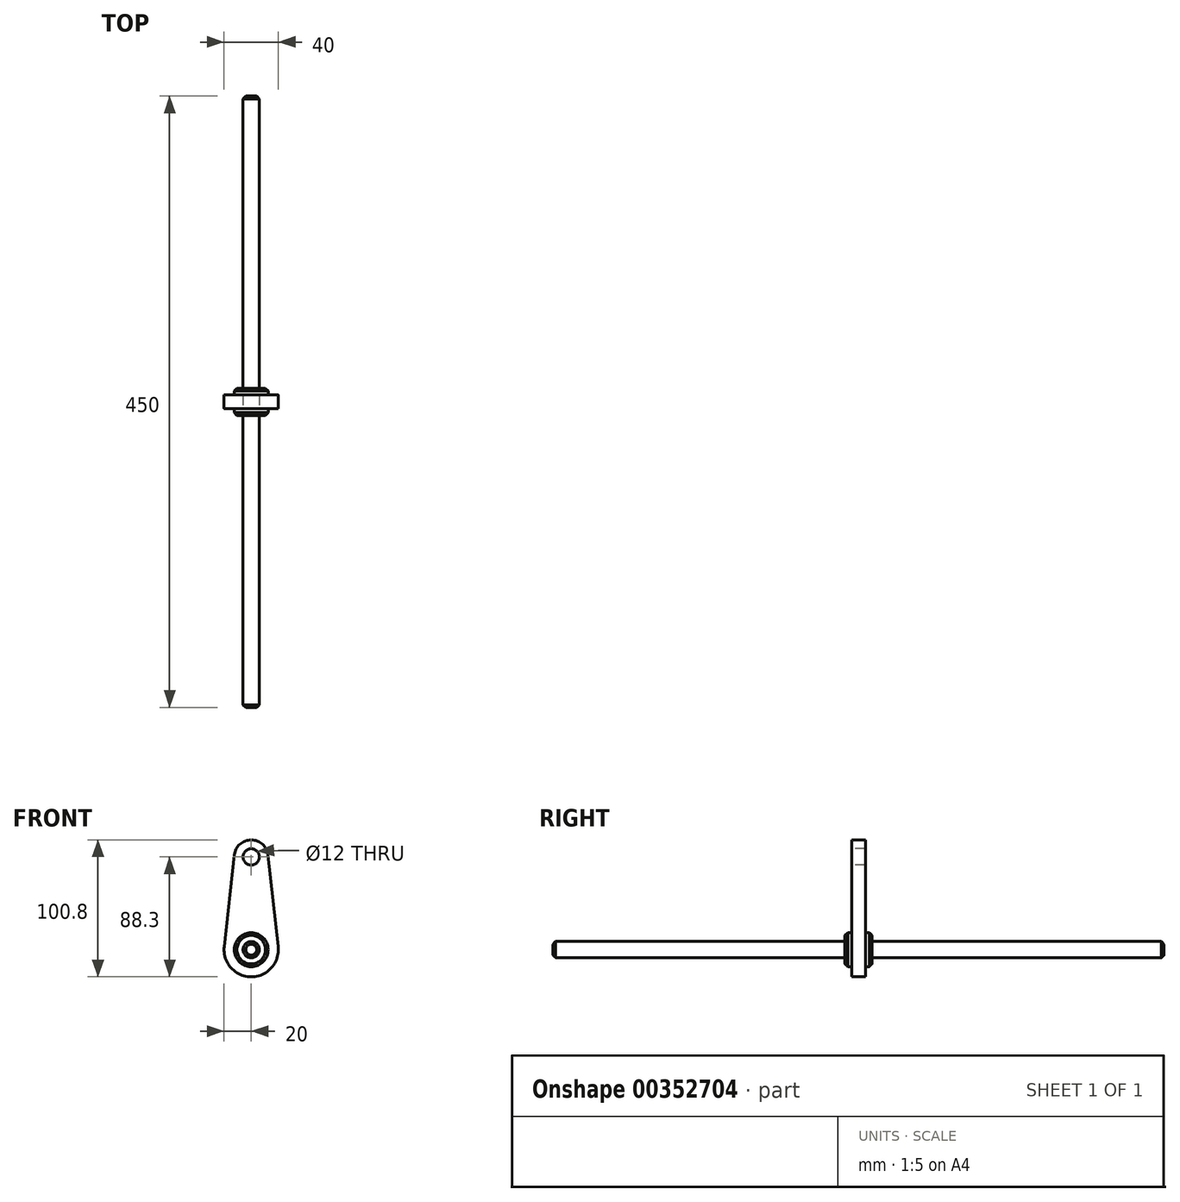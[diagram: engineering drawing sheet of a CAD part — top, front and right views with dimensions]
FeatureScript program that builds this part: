
annotation { "Feature Type Name" : "Feature", "Feature Type Description" : "" }
export const myFeature = defineFeature(function(context is Context, id is Id, definition is map)
    precondition{}
    {
        {
            var Q0;
            Q0=qCreatedBy(makeId("Front.planeOp"),FACE);
            var sketch = newSketch(context, id + "F0", { "sketchPlane" : qUnion([Q0])});
            skCircle(sketch, "E0", {"center": v(0, 0) * mm, "radius": 6 * mm});
            skSolve(sketch);
        }
        {
            var Q0;
            Q0 = qSketchRegion(id + "F0", true);
            extrude(context, id + "F1", {"entities" : qUnion([Q0]), "depth" : 450 * mm});
        }
        {
            var Q0;
            Q0=makeQuery(id+"F1.opExtrude","CAP_EDGE",EDGE,{"disambiguationData":[OSD([sQuery(id+"F0.wireOp",EDGE,"E0")])],"isStart":false});
            var Q1;
            Q1=makeQuery(id+"F1.opExtrude","CAP_EDGE",EDGE,{"disambiguationData":[OSD([sQuery(id+"F0.wireOp",EDGE,"E0")])],"isStart":true});
            chamfer(context, id + "F2", {"entities" : qUnion([Q0, Q1]), "width" : 2 * mm, "tangentPropagation" : true});
        }
        {
            var Q0;
            Q0=qCreatedBy(makeId("Front.planeOp"),FACE);
            cPlane(context, id + "F3", {"entities" : qUnion([Q0]), "cplaneType" : CPlaneType.OFFSET, "offset" : 225 * mm, "width" : 150 * mm, "height" : 150 * mm});
        }
        {
            var Q0;
            Q0=qCreatedBy(id+"F3.planeOp",FACE);
            var sketch = newSketch(context, id + "F4", { "sketchPlane" : qUnion([Q0])});
            skCircle(sketch, "E1", {"center": v(0, 0) * mm, "radius": 12.5 * mm});
            skSolve(sketch);
        }
        {
            var Q0;
            Q0 = qSketchRegion(id + "F4", true);
            extrude(context, id + "F5", {"entities" : qUnion([Q0]), "operationType" : NewBodyOperationType.ADD, "endBound" : BoundingType.SYMMETRIC, "depth" : 20 * mm});
        }
        {
            var Q0;
            Q0=makeQuery(id+"F5.opExtrude","CAP_EDGE",EDGE,{"disambiguationData":[OSD([sQuery(id+"F4.wireOp",EDGE,"E1")])],"isStart":false});
            var Q1;
            Q1=makeQuery(id+"F5.opExtrude","CAP_EDGE",EDGE,{"disambiguationData":[OSD([sQuery(id+"F4.wireOp",EDGE,"E1")])],"isStart":true});
            chamfer(context, id + "F6", {"entities" : qUnion([Q0, Q1]), "width" : 2 * mm, "tangentPropagation" : true});
        }
        {
            var Q0;
            Q0=qCreatedBy(id+"F3.planeOp",FACE);
            var sketch = newSketch(context, id + "F7", { "sketchPlane" : qUnion([Q0])});
            skCircle(sketch, "E2", {"center": v(0, 0) * mm, "radius": 20 * mm});
            skCircle(sketch, "E3", {"center": v(0, 68.3) * mm, "radius": 12.5 * mm});
            skLineSegment(sketch, "E4", {"start": v(-12.43, 69.6) * mm, "end": v(-19.88, 2.2) * mm});
            skLineSegment(sketch, "E5", {"start": v(12.43, 69.6) * mm, "end": v(20.12, 0) * mm});
            skPoint(sketch, "E6", {"position": v(2.61, 41.8) * mm});
            skSolve(sketch);
        }
        {
            var Q0;
            Q0 = qSketchRegion(id + "F7", true);
            extrude(context, id + "F8", {"entities" : qUnion([Q0]), "operationType" : NewBodyOperationType.ADD, "endBound" : BoundingType.SYMMETRIC, "depth" : 10 * mm});
        }
        {
            var Q0;
            Q0=makeQuery(id+"F8.opExtrude","CAP_FACE",FACE,{"disambiguationData":[OSD([sQuery(id+"F7.wireOp",EDGE,"E2"),sQuery(id+"F7.wireOp",EDGE,"E3"),sQuery(id+"F7.wireOp",EDGE,"E4"),sQuery(id+"F7.wireOp",EDGE,"E5")])],"isStart":false});
            var sketch = newSketch(context, id + "F9", { "sketchPlane" : qUnion([Q0])});
            skPoint(sketch, "E7", {"position": v(0, 68.3) * mm});
            skSolve(sketch);
        }
        {
            var Q0;
            Q0=sQuery(id+"F9.wireOp",VERTEX,"E7");
            var Q1;
            Q1=makeQuery(id+"F1.opExtrude","SWEPT_BODY",BODY,{"disambiguationData":[OSD([sQuery(id+"F0.wireOp",EDGE,"E0")])]});
            hole(context, id + "F10", {"style" : HoleStyle.SIMPLE, "endStyle" : HoleEndStyle.BLIND, "holeDiameter" : 12 * mm, "holeDepth" : 30 * mm, "isTappedThrough" : true, "tappedDepth" : 12 * mm, "tapClearance" : 3, "locations" : qUnion([Q0]), "scope" : qUnion([Q1])});
        }
    });
